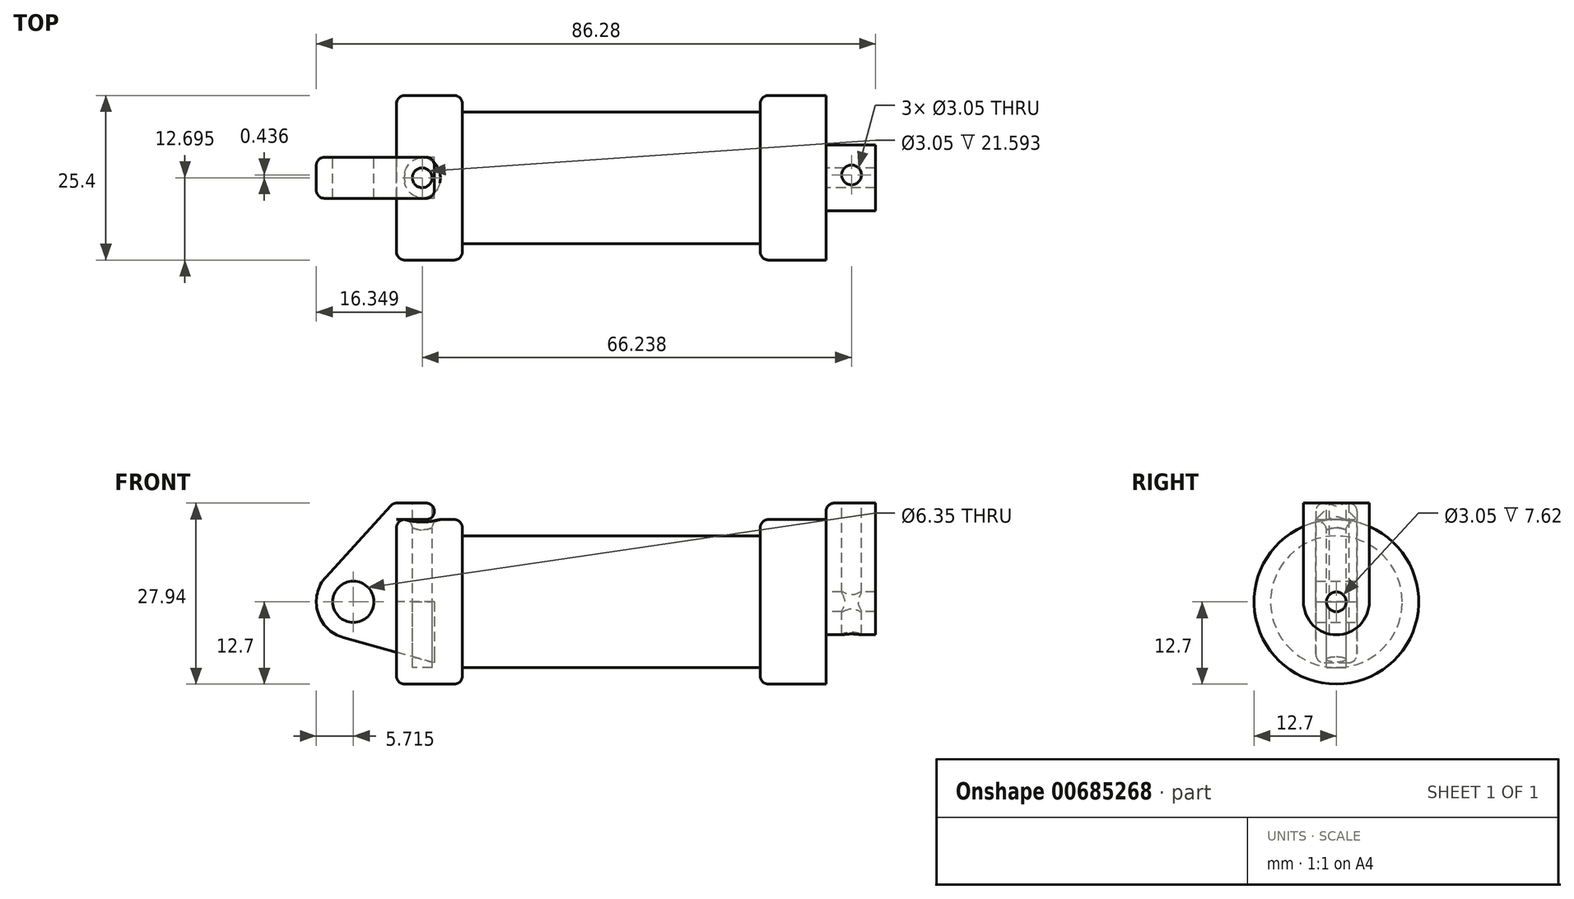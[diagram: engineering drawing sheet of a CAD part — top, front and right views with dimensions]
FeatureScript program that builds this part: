
annotation { "Feature Type Name" : "Feature", "Feature Type Description" : "" }
export const myFeature = defineFeature(function(context is Context, id is Id, definition is map)
    precondition{}
    {
        {
            var Q0;
            Q0=qCreatedBy(makeId("Front.planeOp"),FACE);
            var sketch = newSketch(context, id + "F0", { "sketchPlane" : qUnion([Q0])});
            skLineSegment(sketch, "E0", {"start": v(0, 0) * mm, "end": v(0, 12.7) * mm});
            skLineSegment(sketch, "E1", {"start": v(0, 12.7) * mm, "end": v(10.16, 12.7) * mm});
            skLineSegment(sketch, "E2", {"start": v(10.16, 12.7) * mm, "end": v(10.16, 10.16) * mm});
            skLineSegment(sketch, "E3", {"start": v(10.16, 10.16) * mm, "end": v(56.13, 10.16) * mm});
            skLineSegment(sketch, "E4", {"start": v(56.13, 10.16) * mm, "end": v(56.13, 12.7) * mm});
            skLineSegment(sketch, "E5", {"start": v(56.13, 12.7) * mm, "end": v(66.3, 12.7) * mm});
            skLineSegment(sketch, "E6", {"start": v(66.3, 12.7) * mm, "end": v(66.3, 0) * mm});
            skLineSegment(sketch, "E7", {"start": v(66.3, 0) * mm, "end": v(0, 0) * mm});
            skLineSegment(sketch, "E8", {"start": v(5.84, 15.24) * mm, "end": v(-0.5, 15.24) * mm});
            skLineSegment(sketch, "E9", {"start": v(-0.5, 15.24) * mm, "end": v(-10.88, 3.85) * mm});
            skLineSegment(sketch, "E10", {"start": v(0, 0) * mm, "end": v(-6.65, 0) * mm});
            skCircle(sketch, "E11", {"center": v(-6.65, 0) * mm, "radius": 5.72 * mm});
            skCircle(sketch, "E12", {"center": v(-6.65, 0) * mm, "radius": 3.18 * mm});
            skLineSegment(sketch, "E13", {"start": v(5.84, 15.24) * mm, "end": v(5.84, -9.4) * mm});
            skLineSegment(sketch, "E14", {"start": v(5.84, -9.4) * mm, "end": v(-8.18, -5.5) * mm});
            skSolve(sketch);
        }
        {
            var Q0;
            {var subQ0=sQuery(id+"F0.wireOp",EDGE,"E0");Q0=makeQuery(id+"F0.imprint","IMPRINT",FACE,{"disambiguationData":[TD([[makeQuery(id+"F0.imprint","IMPRINT",EDGE,{"derivedFrom":subQ0}),-1.0]])]});}
            var Q1;
            {var subQ0=sQuery(id+"F0.wireOp",EDGE,"E2");Q1=makeQuery(id+"F0.imprint","IMPRINT",FACE,{"disambiguationData":[TD([[makeQuery(id+"F0.imprint","IMPRINT",EDGE,{"derivedFrom":subQ0}),-1.0]])]});}
            var Q2;
            Q2=sQuery(id+"F0.wireOp",EDGE,"E7");
            revolve(context, id + "F1", {"entities" : qUnion([Q0, Q1]), "axis" : qUnion([Q2]), "revolveType" : RevolveType.FULL});
        }
        {
            var Q0;
            {var subQ1=sQuery(id+"F0.wireOp",EDGE,"E0");Q0=makeQuery(id+"F0.imprint","IMPRINT",FACE,{"disambiguationData":[TD([[makeQuery(id+"F0.imprint","IMPRINT",EDGE,{"derivedFrom":subQ1}),1.0]])]});}
            var Q1;
            {var subQ0=sQuery(id+"F0.wireOp",EDGE,"E14");Q1=makeQuery(id+"F0.imprint","IMPRINT",FACE,{"disambiguationData":[TD([[makeQuery(id+"F0.imprint","IMPRINT",EDGE,{"derivedFrom":subQ0}),-1.0]])]});}
            var Q2;
            {var subQ5=sQuery(id+"F0.wireOp",EDGE,"E12");Q2=makeQuery(id+"F0.imprint","IMPRINT",FACE,{"disambiguationData":[TD([[makeQuery(id+"F0.imprint","IMPRINT",EDGE,{"derivedFrom":subQ5}),-1.0]])]});}
            extrude(context, id + "F2", {"entities" : qUnion([Q0, Q1, Q2]), "endBound" : BoundingType.SYMMETRIC, "depth" : 6.35 * mm, "offsetDistance" : 25.4 * mm});
        }
        {
            var Q0;
            Q0=makeQuery(id+"F1.opRevolve","SWEPT_FACE",FACE,{"disambiguationData":[OSD([sQuery(id+"F0.wireOp",EDGE,"E6")])]});
            var sketch = newSketch(context, id + "F3", { "sketchPlane" : qUnion([Q0])});
            skCircle(sketch, "E15", {"center": v(0, 0) * mm, "radius": 5.08 * mm});
            skCircle(sketch, "E16", {"center": v(0, 0) * mm, "radius": 1.52 * mm});
            skLineSegment(sketch, "E17", {"start": v(-5.08, 0) * mm, "end": v(-5.08, 15.24) * mm});
            skLineSegment(sketch, "E18", {"start": v(5.08, 0) * mm, "end": v(5.08, 15.24) * mm});
            skLineSegment(sketch, "E19", {"start": v(5.08, 15.24) * mm, "end": v(-5.08, 15.24) * mm});
            skSolve(sketch);
        }
        {
            var Q0;
            {var subQ0=sQuery(id+"F3.wireOp",EDGE,"E17");var subQ1=sQuery(id+"F3.wireOp",EDGE,"E15");var subQ2=makeQuery(id+"F3.imprint","INTERSECT",VERTEX,{"derivedFrom":[subQ1,subQ0]});Q0=makeQuery(id+"F3.imprint","IMPRINT",FACE,{"disambiguationData":[TD([[makeQuery(id+"F3.imprint","IMPRINT",EDGE,{"disambiguationData":[TD([[subQ2,1.0]])],"derivedFrom":subQ1}),-1.0]])]});}
            var Q1;
            {var subQ0=sQuery(id+"F3.wireOp",EDGE,"E19");Q1=makeQuery(id+"F3.imprint","IMPRINT",FACE,{"disambiguationData":[TD([[makeQuery(id+"F3.imprint","IMPRINT",EDGE,{"derivedFrom":subQ0}),1.0]])]});}
            var Q2;
            Q2=makeQuery(id+"F3.imprint","IMPRINT",FACE,{"disambiguationData":[TD([[makeQuery(id+"F3.imprint","IMPRINT",EDGE,{"derivedFrom":sQuery(id+"F3.wireOp",EDGE,"E16")}),-1.0]])]});
            extrude(context, id + "F4", {"entities" : qUnion([Q0, Q1, Q2]), "operationType" : NewBodyOperationType.ADD, "depth" : 7.62 * mm, "offsetDistance" : 25.4 * mm});
        }
        {
            var Q0;
            Q0=makeQuery(id+"F4.opExtrude","SWEPT_FACE",FACE,{"disambiguationData":[OSD([sQuery(id+"F3.wireOp",EDGE,"E19")])]});
            var sketch = newSketch(context, id + "F5", { "sketchPlane" : qUnion([Q0])});
            skSolve(sketch);
        }
        {
            var Q0;
            {var subQ0=sQuery(id+"F3.wireOp",EDGE,"E19");Q0=makeQuery(id+"F5.imprint","IMPRINT",FACE,{"disambiguationData":[TD([[makeQuery(id+"F5.imprint","IMPRINT",EDGE,{"derivedFrom":makeQuery(id+"F4.opExtrude","CAP_EDGE",EDGE,{"disambiguationData":[OSD([subQ0])],"isStart":true})}),1.0]])]});}
            var sketch = newSketch(context, id + "F6", { "sketchPlane" : qUnion([Q0])});
            skCircle(sketch, "E20", {"center": v(3.98, 0) * mm, "radius": 1.52 * mm});
            skCircle(sketch, "E21", {"center": v(70.22, 0.43) * mm, "radius": 1.52 * mm});
            skSolve(sketch);
        }
        {
            var Q0;
            Q0=makeQuery(id+"F6.imprint","IMPRINT",FACE,{"disambiguationData":[TD([[makeQuery(id+"F6.imprint","IMPRINT",EDGE,{"derivedFrom":sQuery(id+"F6.wireOp",EDGE,"E21")}),1.0]])]});
            var Q1;
            Q1=makeQuery(id+"F6.imprint","IMPRINT",FACE,{"disambiguationData":[TD([[makeQuery(id+"F6.imprint","IMPRINT",EDGE,{"derivedFrom":sQuery(id+"F6.wireOp",EDGE,"E20")}),1.0]])]});
            extrude(context, id + "F7", {"entities" : qUnion([Q0, Q1]), "operationType" : NewBodyOperationType.REMOVE, "oppositeDirection" : true, "depth" : 25.4 * mm, "offsetDistance" : 25.4 * mm});
        }
        {
            var Q0;
            Q0 = qSketchRegion(id + "F6", true);
            extrude(context, id + "F8", {"entities" : qUnion([Q0]), "operationType" : NewBodyOperationType.REMOVE, "oppositeDirection" : true, "depth" : 25.4 * mm, "offsetDistance" : 25.4 * mm});
        }
        {
            var Q0;
            Q0=makeQuery(id+"F2.opExtrude","CAP_EDGE",EDGE,{"disambiguationData":[OSD([sQuery(id+"F0.wireOp",EDGE,"E8")])],"isStart":false});
            var Q1;
            Q1=makeQuery(id+"F1.opRevolve","SWEPT_FACE",FACE,{"disambiguationData":[OSD([sQuery(id+"F0.wireOp",EDGE,"E1")])]});
            var Q2;
            Q2=makeQuery(id+"F1.opRevolve","SWEPT_EDGE",EDGE,{"disambiguationData":[OSD([sQuery(id+"F0.wireOp",EDGE,"E1"),sQuery(id+"F0.wireOp",EDGE,"E2")])]});
            var Q3;
            Q3=makeQuery(id+"F4.opExtrude","CAP_EDGE",EDGE,{"disambiguationData":[OSD([sQuery(id+"F3.wireOp",EDGE,"E19")])],"isStart":true});
            var Q4;
            Q4=makeQuery(id+"F1.opRevolve","SWEPT_EDGE",EDGE,{"disambiguationData":[OSD([sQuery(id+"F0.wireOp",EDGE,"E4"),sQuery(id+"F0.wireOp",EDGE,"E5")])]});
            var Q5;
            Q5=makeQuery(id+"F2.opExtrude","CAP_EDGE",EDGE,{"disambiguationData":[OSD([sQuery(id+"F0.wireOp",EDGE,"E8")])],"isStart":true});
            var Q6;
            Q6=makeQuery(id+"F2.opExtrude","SWEPT_FACE",FACE,{"disambiguationData":[OSD([sQuery(id+"F0.wireOp",EDGE,"E9")])]});
            fillet(context, id + "F9", {"entities" : qUnion([Q0, Q1, Q2, Q3, Q4, Q5, Q6]), "radius" : 1.27 * mm, "tangentPropagation" : true, "allowEdgeOverflow" : false});
        }
        {
            var Q0;
            Q0=makeQuery(id+"F2.opExtrude","SWEPT_EDGE",EDGE,{"disambiguationData":[OSD([sQuery(id+"F0.wireOp",EDGE,"E8"),sQuery(id+"F0.wireOp",EDGE,"E13")])]});
            var Q1;
            {var subQ0=sQuery(id+"F0.wireOp",EDGE,"E13");Q1=makeQuery(id+"F2.opExtrude","CAP_EDGE",EDGE,{"disambiguationData":[OSD([subQ0]),TDD([makeQuery(id+"F0.imprint","IMPRINT",EDGE,{"disambiguationData":[TD([[makeQuery(id+"F0.imprint","INTERSECT",VERTEX,{"derivedFrom":[sQuery(id+"F0.wireOp",EDGE,"E8"),subQ0]}),-1.0]])],"derivedFrom":subQ0})])],"isStart":true});}
            var Q2;
            Q2=makeQuery(id+"F2.opExtrude","SWEPT_EDGE",EDGE,{"disambiguationData":[OSD([sQuery(id+"F0.wireOp",EDGE,"E1"),sQuery(id+"F0.wireOp",EDGE,"E13")])]});
            var Q3;
            {var subQ0=sQuery(id+"F0.wireOp",EDGE,"E13");var subQ1=sQuery(id+"F0.wireOp",EDGE,"E8");Q3=makeQuery(id+"F9.opFillet","BLEND_EDGE",EDGE,{"blendedFrom":[makeQuery(id+"F2.opExtrude","CAP_EDGE",EDGE,{"disambiguationData":[OSD([subQ1])],"isStart":true}),makeQuery(id+"F2.opExtrude","SWEPT_FACE",FACE,{"disambiguationData":[OSD([subQ0]),TDD([makeQuery(id+"F0.imprint","IMPRINT",EDGE,{"disambiguationData":[TD([[makeQuery(id+"F0.imprint","INTERSECT",VERTEX,{"derivedFrom":[subQ1,subQ0]}),-1.0]])],"derivedFrom":subQ0})])]})],"blendedInto":[makeQuery(id+"F2.opExtrude","SWEPT_FACE",FACE,{"disambiguationData":[OSD([subQ0]),TDD([makeQuery(id+"F0.imprint","IMPRINT",EDGE,{"disambiguationData":[TD([[makeQuery(id+"F0.imprint","INTERSECT",VERTEX,{"derivedFrom":[subQ1,subQ0]}),-1.0]])],"derivedFrom":subQ0})])]})]});}
            var Q4;
            {var subQ0=sQuery(id+"F0.wireOp",EDGE,"E13");Q4=makeQuery(id+"F2.opExtrude","CAP_EDGE",EDGE,{"disambiguationData":[OSD([subQ0]),TDD([makeQuery(id+"F0.imprint","IMPRINT",EDGE,{"disambiguationData":[TD([[makeQuery(id+"F0.imprint","INTERSECT",VERTEX,{"derivedFrom":[sQuery(id+"F0.wireOp",EDGE,"E8"),subQ0]}),-1.0]])],"derivedFrom":subQ0})])],"isStart":false});}
            var Q5;
            {var subQ0=sQuery(id+"F0.wireOp",EDGE,"E13");var subQ1=sQuery(id+"F0.wireOp",EDGE,"E8");Q5=makeQuery(id+"F9.opFillet","BLEND_EDGE",EDGE,{"blendedFrom":[makeQuery(id+"F2.opExtrude","CAP_EDGE",EDGE,{"disambiguationData":[OSD([subQ1])],"isStart":false}),makeQuery(id+"F2.opExtrude","SWEPT_FACE",FACE,{"disambiguationData":[OSD([subQ0]),TDD([makeQuery(id+"F0.imprint","IMPRINT",EDGE,{"disambiguationData":[TD([[makeQuery(id+"F0.imprint","INTERSECT",VERTEX,{"derivedFrom":[subQ1,subQ0]}),-1.0]])],"derivedFrom":subQ0})])]})],"blendedInto":[makeQuery(id+"F2.opExtrude","SWEPT_FACE",FACE,{"disambiguationData":[OSD([subQ0]),TDD([makeQuery(id+"F0.imprint","IMPRINT",EDGE,{"disambiguationData":[TD([[makeQuery(id+"F0.imprint","INTERSECT",VERTEX,{"derivedFrom":[subQ1,subQ0]}),-1.0]])],"derivedFrom":subQ0})])]})]});}
            fillet(context, id + "F10", {"entities" : qUnion([Q0, Q1, Q2, Q3, Q4, Q5]), "radius" : 1.27 * mm, "tangentPropagation" : true, "allowEdgeOverflow" : false});
        }
    });
